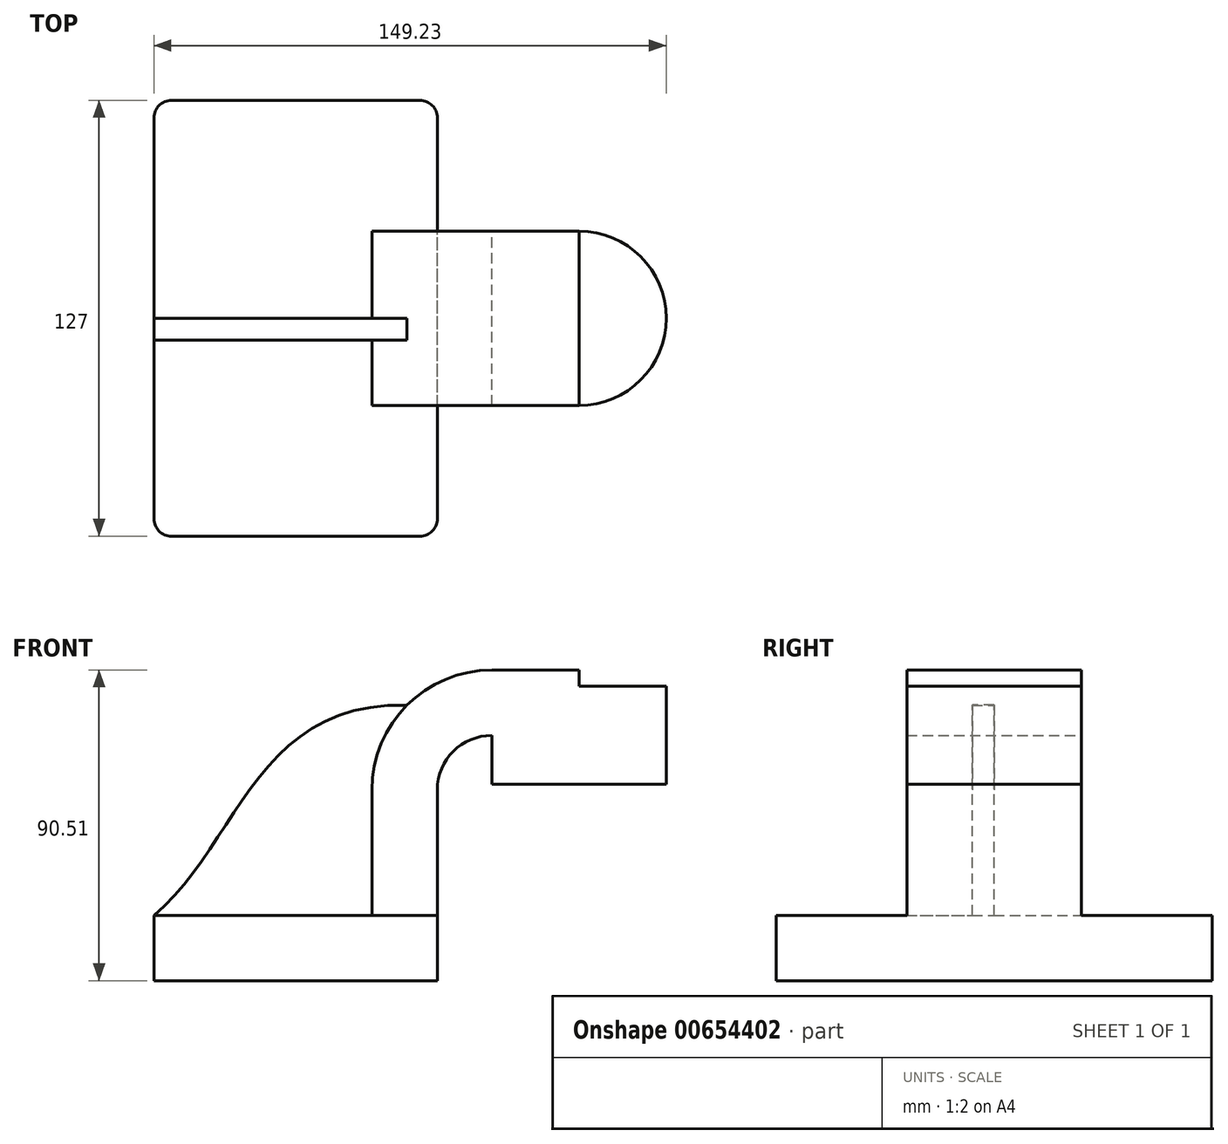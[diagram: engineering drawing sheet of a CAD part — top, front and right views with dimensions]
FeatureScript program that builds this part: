
annotation { "Feature Type Name" : "Feature", "Feature Type Description" : "" }
export const myFeature = defineFeature(function(context is Context, id is Id, definition is map)
    precondition{}
    {
        {
            var Q0;
            Q0=qCreatedBy(makeId("Front.planeOp"),FACE);
            var sketch = newSketch(context, id + "F0", { "sketchPlane" : qUnion([Q0])});
            skLineSegment(sketch, "E0.bottom", {"start": v(41.27, 9.53) * mm, "end": v(-41.28, 9.53) * mm});
            skLineSegment(sketch, "E0.top", {"start": v(41.28, -9.52) * mm, "end": v(-41.27, -9.52) * mm});
            skLineSegment(sketch, "E0.left", {"start": v(41.28, 9.53) * mm, "end": v(41.28, -9.52) * mm});
            skLineSegment(sketch, "E0.right", {"start": v(-41.28, 9.53) * mm, "end": v(-41.27, -9.52) * mm});
            skPoint(sketch, "E0.middle", {"position": v(0, 0) * mm});
            skLineSegment(sketch, "E1.bottom", {"start": v(107.95, 47.64) * mm, "end": v(57.15, 47.64) * mm});
            skLineSegment(sketch, "E1.top", {"start": v(107.95, 76.21) * mm, "end": v(57.15, 76.21) * mm});
            skLineSegment(sketch, "E1.left", {"start": v(107.95, 47.64) * mm, "end": v(107.95, 76.21) * mm});
            skLineSegment(sketch, "E1.right", {"start": v(57.15, 47.64) * mm, "end": v(57.15, 76.21) * mm});
            skPoint(sketch, "E1.middle", {"position": v(82.55, 61.93) * mm});
            skLineSegment(sketch, "E2", {"start": v(41.28, 9.53) * mm, "end": v(41.28, 46.05) * mm});
            skArc(sketch, "E3", {"start": v(41.27, 46.05) * mm, "mid": v(45.92, 57.28) * mm, "end": v(57.15, 61.93) * mm});
            skPoint(sketch, "E3.centerSnap0", {"position": v(57.15, 61.93) * mm});
            skLineSegment(sketch, "E4", {"start": v(57.15, 61.93) * mm, "end": v(82.55, 61.93) * mm});
            skLineSegment(sketch, "E5.0", {"start": v(57.15, 80.98) * mm, "end": v(82.55, 80.98) * mm});
            skArc(sketch, "E5.1", {"start": v(22.22, 46.05) * mm, "mid": v(32.45, 70.75) * mm, "end": v(57.15, 80.98) * mm});
            skLineSegment(sketch, "E5.2", {"start": v(22.23, 9.53) * mm, "end": v(22.23, 46.05) * mm});
            skLineSegment(sketch, "E6", {"start": v(82.55, 80.98) * mm, "end": v(82.55, 47.64) * mm});
            skFitSpline(sketch, "E7", {"points": [v(-41.28, 9.52) * mm, v(32.45, 70.75) * mm], "startDerivative": vector(73.73, 61.22) * mm, "endDerivative": vector(133.29, -3.17) * mm});
            skSolve(sketch);
        }
        {
            var Q0;
            Q0=makeQuery(id+"F0.imprint","IMPRINT",FACE,{"disambiguationData":[TD([[makeQuery(id+"F0.imprint","IMPRINT",EDGE,{"derivedFrom":sQuery(id+"F0.wireOp",EDGE,"E0.top")}),-1.0]])]});
            extrude(context, id + "F1", {"entities" : qUnion([Q0]), "endBound" : BoundingType.SYMMETRIC, "depth" : 127 * mm, "offsetDistance" : 25.4 * mm});
        }
        {
            var Q0;
            {var subQ0=sQuery(id+"F0.wireOp",EDGE,"E2");Q0=makeQuery(id+"F0.imprint","IMPRINT",FACE,{"disambiguationData":[TD([[makeQuery(id+"F0.imprint","IMPRINT",EDGE,{"derivedFrom":subQ0}),1.0]])]});}
            var Q1;
            {var subQ5=sQuery(id+"F0.wireOp",EDGE,"E4");Q1=makeQuery(id+"F0.imprint","IMPRINT",FACE,{"disambiguationData":[TD([[makeQuery(id+"F0.imprint","IMPRINT",EDGE,{"derivedFrom":subQ5}),1.0]])]});}
            var Q2;
            {var subQ5=sQuery(id+"F0.wireOp",EDGE,"E4");Q2=makeQuery(id+"F0.imprint","IMPRINT",FACE,{"disambiguationData":[TD([[makeQuery(id+"F0.imprint","IMPRINT",EDGE,{"derivedFrom":subQ5}),-1.0]])]});}
            extrude(context, id + "F2", {"entities" : qUnion([Q0, Q1, Q2]), "operationType" : NewBodyOperationType.ADD, "endBound" : BoundingType.SYMMETRIC, "depth" : 50.8 * mm, "offsetDistance" : 25.4 * mm});
        }
        {
            var Q0;
            {var subQ2=sQuery(id+"F0.wireOp",EDGE,"E5.2");Q0=makeQuery(id+"F0.imprint","IMPRINT",FACE,{"disambiguationData":[TD([[makeQuery(id+"F0.imprint","IMPRINT",EDGE,{"derivedFrom":subQ2}),1.0]])]});}
            extrude(context, id + "F3", {"entities" : qUnion([Q0]), "operationType" : NewBodyOperationType.ADD, "depth" : 6.35 * mm, "offsetDistance" : 25.4 * mm});
        }
        {
            var Q0;
            {var subQ0=sQuery(id+"F0.wireOp",EDGE,"E1.left");Q0=makeQuery(id+"F0.imprint","IMPRINT",FACE,{"disambiguationData":[TD([[makeQuery(id+"F0.imprint","IMPRINT",EDGE,{"derivedFrom":subQ0}),1.0]])]});}
            var Q1;
            Q1=sQuery(id+"F0.wireOp",EDGE,"E6");
            revolve(context, id + "F4", {"operationType" : NewBodyOperationType.ADD, "entities" : qUnion([Q0]), "axis" : qUnion([Q1]), "revolveType" : RevolveType.FULL});
        }
        {
            var Q0;
            Q0=makeQuery(id+"F1.opExtrude","CAP_EDGE",EDGE,{"disambiguationData":[OSD([sQuery(id+"F0.wireOp",EDGE,"E0.right")])],"isStart":false});
            var Q1;
            Q1=makeQuery(id+"F1.opExtrude","CAP_EDGE",EDGE,{"disambiguationData":[OSD([sQuery(id+"F0.wireOp",EDGE,"E0.left")])],"isStart":false});
            var Q2;
            Q2=makeQuery(id+"F1.opExtrude","CAP_EDGE",EDGE,{"disambiguationData":[OSD([sQuery(id+"F0.wireOp",EDGE,"E0.right")])],"isStart":true});
            var Q3;
            Q3=makeQuery(id+"F1.opExtrude","CAP_EDGE",EDGE,{"disambiguationData":[OSD([sQuery(id+"F0.wireOp",EDGE,"E0.left")])],"isStart":true});
            fillet(context, id + "F5", {"entities" : qUnion([Q0, Q1, Q2, Q3]), "radius" : 5.08 * mm, "tangentPropagation" : true, "allowEdgeOverflow" : false});
        }
    });
